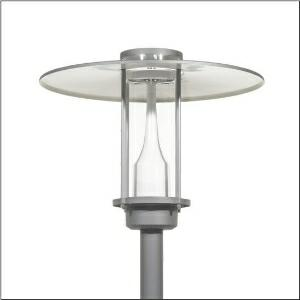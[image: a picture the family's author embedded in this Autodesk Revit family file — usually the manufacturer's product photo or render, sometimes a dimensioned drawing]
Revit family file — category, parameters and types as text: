
# Revit family: city-light_plus_iq___st1_2a_5xa5275kf14hp_140d
name_source: partatom
category: Lighting Fixtures
units: mm (PartAtom-declared; Revit-internal decimal feet)

## family parameters
Cut with Voids When Loaded = No
Host = Face
Light Source = No
Part Type = Normal
Room Calculation Point = No
Round Connector Dimension = Use Diameter
Shared = No

## types (1)
- --- (1 x LED, 4710 lm, 33.6 W, 4000K)
    Apparent Load = 34 VA
    CIE Flux Codes = 22 60 93 97 100
    Color Rendering = 70
    Color Temperature = 4000K
    Default Elevation = 1800 mm
    Description = City-Light Plus iQ, mast luminaire, Module 540 iQ-SR, primary light control with 3 zone facetted reflector, of plastic, silver coated, highly specular, structured, primary optical cover: cover, of PMMA, transparent, light distribution: ST1.2a, light emission: direct distribution, primary light characteristic: asymmetric, installation type: post-top, LED, High Power LED, rated luminous flux: 4.710lm, luminous efficacy: 140lm/W, light colour: 740, colour temperature: 4000K, control gear: iQ Street-Remote, control: pre-setting: logarithmic dimming characteristic, Street-Remote, Auto-Match, Temp-Guard, Lumen-Switch, Night-Set, Smart-Wire, Light-Fading, Desk-Remote (wireless, voltage-free reading and setting of iQ features in the workshop via application-optimized NFC function/RFID function), optimised constant luminous flux control (CLO 2.0), with terminal, 6-pole, max. 2.5mm², mains connection: 230..240V, AC, 50/60Hz, start of lifetime: 34W, end of service life: 36W, reduction: 15W, luminaire housing, upper part, of glass-fibre reinforced polyester, coated, Siteco® metallic grey (DB 702S), diameter: 750mm, height: 590mm, spigot size: d x l = 76 x 70mm (post-top) | with reducer (optional accessory) 60 x 70mm, mounting height: 3..5m, post-top mast mounting element, of diecast aluminium, coated, Siteco® metallic grey (DB 702S), Module 540 iQ-SR, traffic white (RAL 9016), equipment: Power, protection rating (complete): IP65, insulation class (complete): insulation class II (safety insulation), certification: CE, ENEC, VDE, packaging unit: 1 piece

Light Distribution: ST1.2a
    Height = 590 mm
    Lamp = 1 x LED
    Lamp Light Flux = 4710 lm
    Lamp Power = 33.6 W
    Lamp count = 1
    Length = 750 mm
    Luminous efficacy = 140 lm/W
    Manufacturer = Siteco
    ModVariant = No
    Model = 5XA5275KF14HP
    Number of Poles = 1
    OnlyDefault = Yes
    Power Factor = 1
    Product Name = City-Light Plus iQ | ST1.2a
    Product group = mast luminaire | pylon top
    ProductGroupID = 6100
    Protection Class = Protection class II
    Protection Degree = IP 65
    RLX_Detail_Level = 1
    RLX_Emergency_Light_Flux = 0 lm
    RLX_Emergency_Type = 0
    RLX_Emergency_Type_DB = No
    RlxData = <blob elided: 35009 chars, md5=62ef2d71>
    Socket = socket
    Standby Power = 0 W
    System Light Flux = 4710 lm
    System Power = 34 W
    Type Comments = factory setting: luminous flux: 100 % | dim-lin: 254 | 695 mA
    Type Image = l_1006456.jpg
    URL = http://relux.com
    VarID = @adj_193810
    Voltage = 0 V
    Weight = 0.00 kg
    Width = 0 mm  [stored 0 ft]

note: [stored X ft] marks values corroborated as IEEE doubles in the binary element streams (Revit-internal decimal feet)

## geometry (parser evidence)
native form markers: Blend x4, Sweep x11
no freeform markers — native parametric forms only
